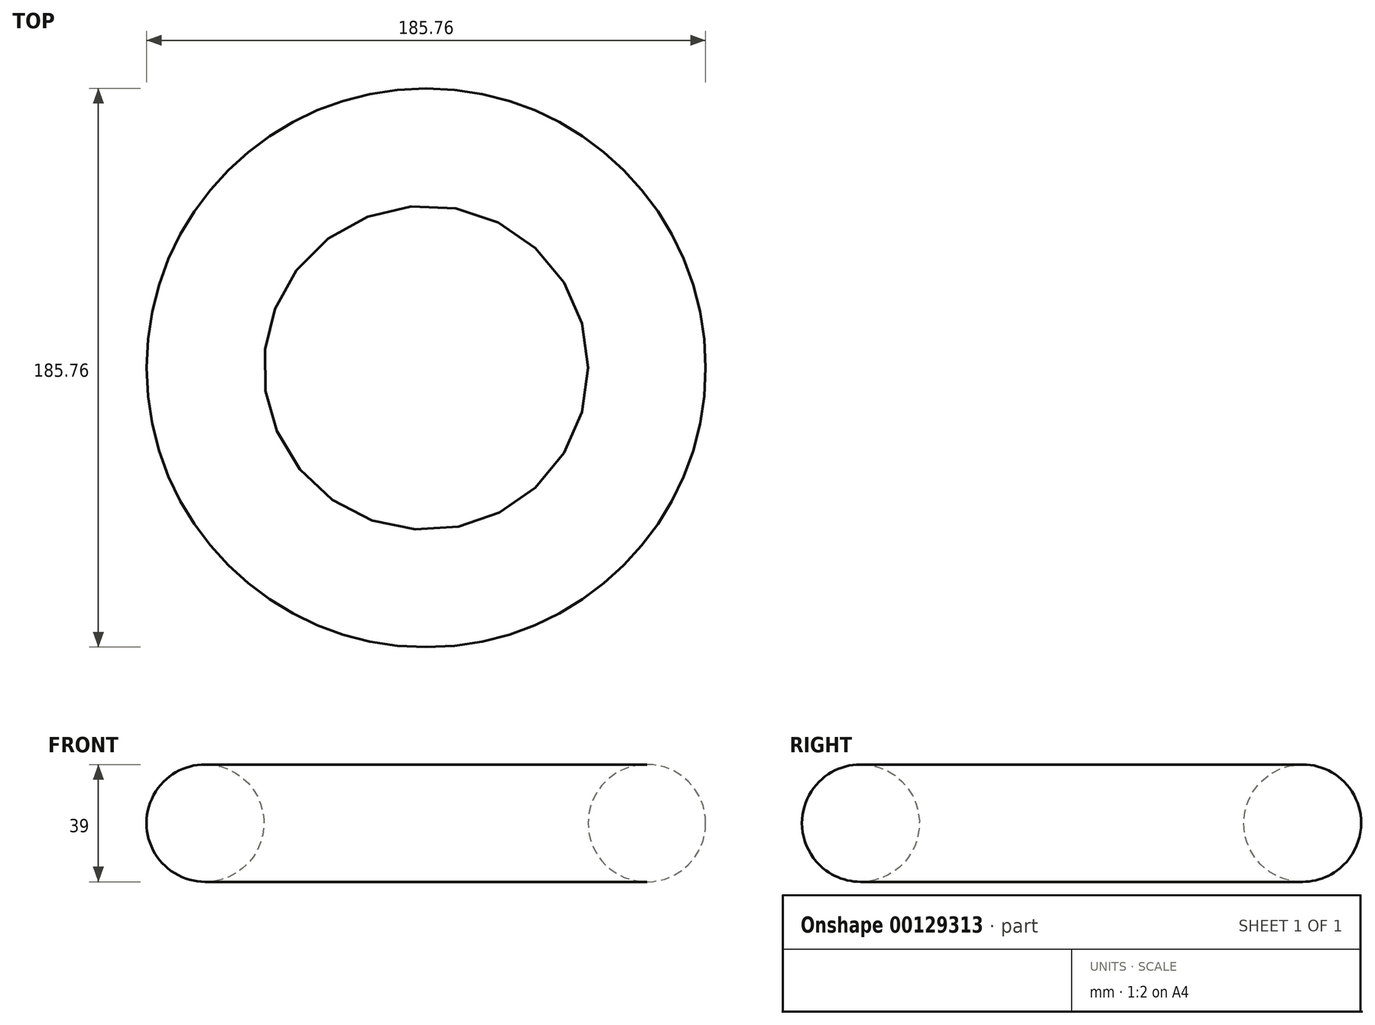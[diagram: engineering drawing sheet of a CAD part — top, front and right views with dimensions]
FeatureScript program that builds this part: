
annotation { "Feature Type Name" : "Feature", "Feature Type Description" : "" }
export const myFeature = defineFeature(function(context is Context, id is Id, definition is map)
    precondition{}
    {
        {
            var Q0;
            Q0=qCreatedBy(makeId("Front.planeOp"),FACE);
            var sketch = newSketch(context, id + "F0", { "sketchPlane" : qUnion([Q0])});
            skCircle(sketch, "E0", {"center": v(73.37, 0) * mm, "radius": 19.5 * mm});
            skLineSegment(sketch, "E1", {"start": v(0, 0) * mm, "end": v(0, -26.62) * mm});
            skSolve(sketch);
        }
        {
            var Q0;
            Q0=makeQuery(id+"F0.imprint","IMPRINT",FACE,{"disambiguationData":[TD([[makeQuery(id+"F0.imprint","IMPRINT",EDGE,{"derivedFrom":sQuery(id+"F0.wireOp",EDGE,"E0")}),1.0]])]});
            var Q1;
            Q1=sQuery(id+"F0.wireOp",EDGE,"E1");
            revolve(context, id + "F1", {"entities" : qUnion([Q0]), "axis" : qUnion([Q1]), "revolveType" : RevolveType.FULL});
        }
    });
